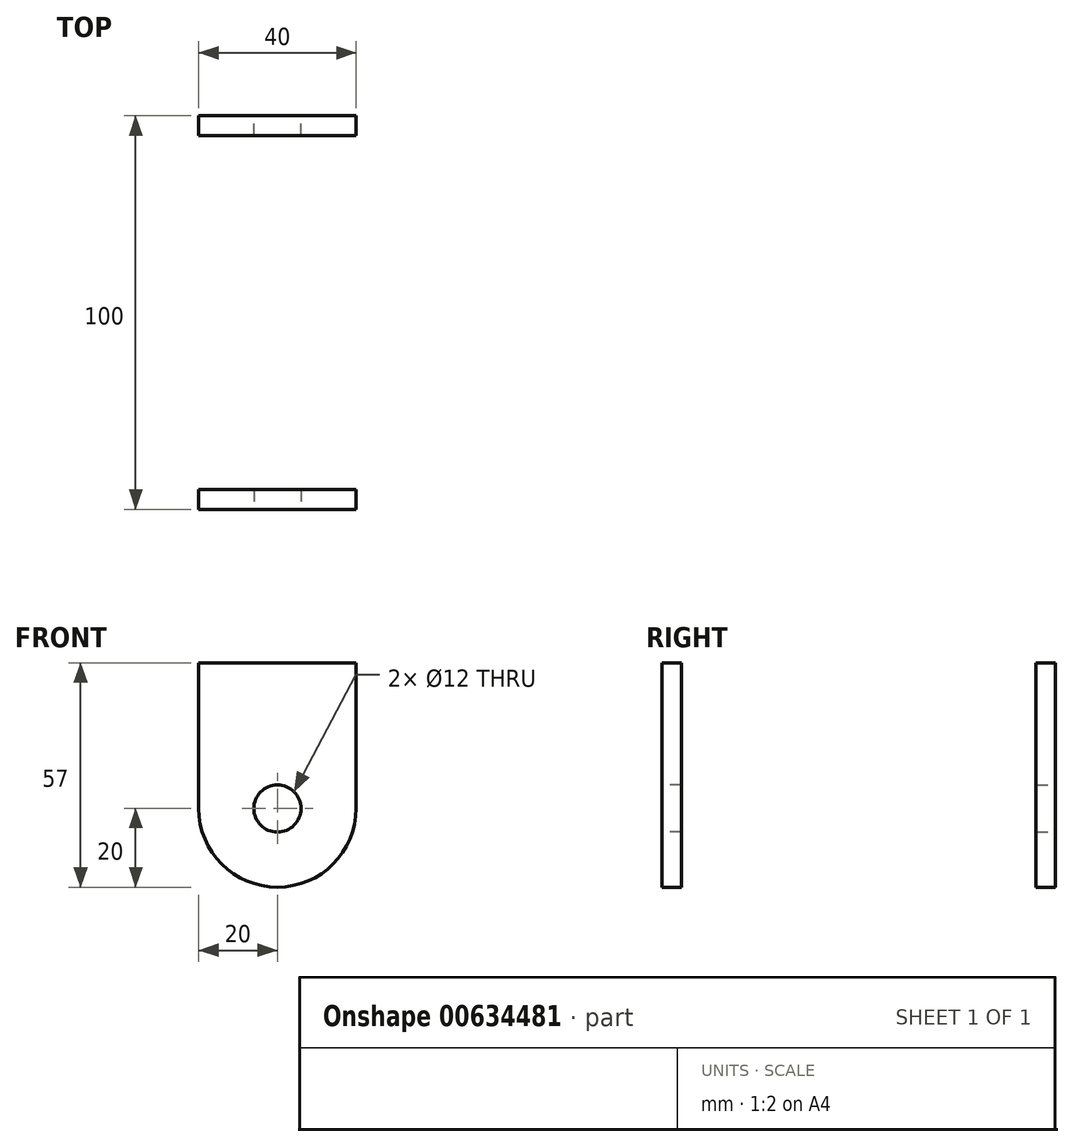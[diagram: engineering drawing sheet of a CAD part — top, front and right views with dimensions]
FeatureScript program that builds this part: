
annotation { "Feature Type Name" : "Feature", "Feature Type Description" : "" }
export const myFeature = defineFeature(function(context is Context, id is Id, definition is map)
    precondition{}
    {
        {
            var Q0;
            Q0=qCreatedBy(makeId("Front.planeOp"),FACE);
            var sketch = newSketch(context, id + "F0", { "sketchPlane" : qUnion([Q0])});
            skLineSegment(sketch, "E0.bottom", {"start": v(20, 18.5) * mm, "end": v(-20, 18.5) * mm});
            skLineSegment(sketch, "E0.left", {"start": v(20, 18.5) * mm, "end": v(20, -18.5) * mm});
            skLineSegment(sketch, "E0.right", {"start": v(-20, 18.5) * mm, "end": v(-20, -18.5) * mm});
            skPoint(sketch, "E0.middle", {"position": v(0, 0) * mm});
            skCircle(sketch, "E1", {"center": v(0, -18.5) * mm, "radius": 6 * mm});
            skArc(sketch, "E2", {"start": v(-20, -18.5) * mm, "mid": v(0, -38.5) * mm, "end": v(20, -18.5) * mm});
            skSolve(sketch);
        }
        {
            var Q0;
            Q0=makeQuery(id+"F0.imprint","IMPRINT",FACE,{"disambiguationData":[TD([[makeQuery(id+"F0.imprint","IMPRINT",EDGE,{"derivedFrom":sQuery(id+"F0.wireOp",EDGE,"E0.bottom")}),1.0]])]});
            extrude(context, id + "F1", {"entities" : qUnion([Q0]), "depth" : 5 * mm, "offsetDistance" : 25 * mm});
        }
        {
            var Q0;
            Q0=qCreatedBy(makeId("Front.planeOp"),FACE);
            cPlane(context, id + "F2", {"entities" : qUnion([Q0]), "cplaneType" : CPlaneType.OFFSET, "offset" : 50 * mm, "width" : 150 * mm, "height" : 150 * mm});
        }
        {
            var Q0;
            Q0=makeQuery(id+"F1.opExtrude","SWEPT_BODY",BODY,{"disambiguationData":[OSD([sQuery(id+"F0.wireOp",EDGE,"E0.bottom"),sQuery(id+"F0.wireOp",EDGE,"E0.left"),sQuery(id+"F0.wireOp",EDGE,"E0.right"),sQuery(id+"F0.wireOp",EDGE,"E1"),sQuery(id+"F0.wireOp",EDGE,"E2")])]});
            var Q1;
            Q1=qCreatedBy(id+"F2.planeOp",FACE);
            mirror(context, id + "F3", {"entities" : qUnion([Q0]), "mirrorPlane" : qUnion([Q1])});
        }
    });
